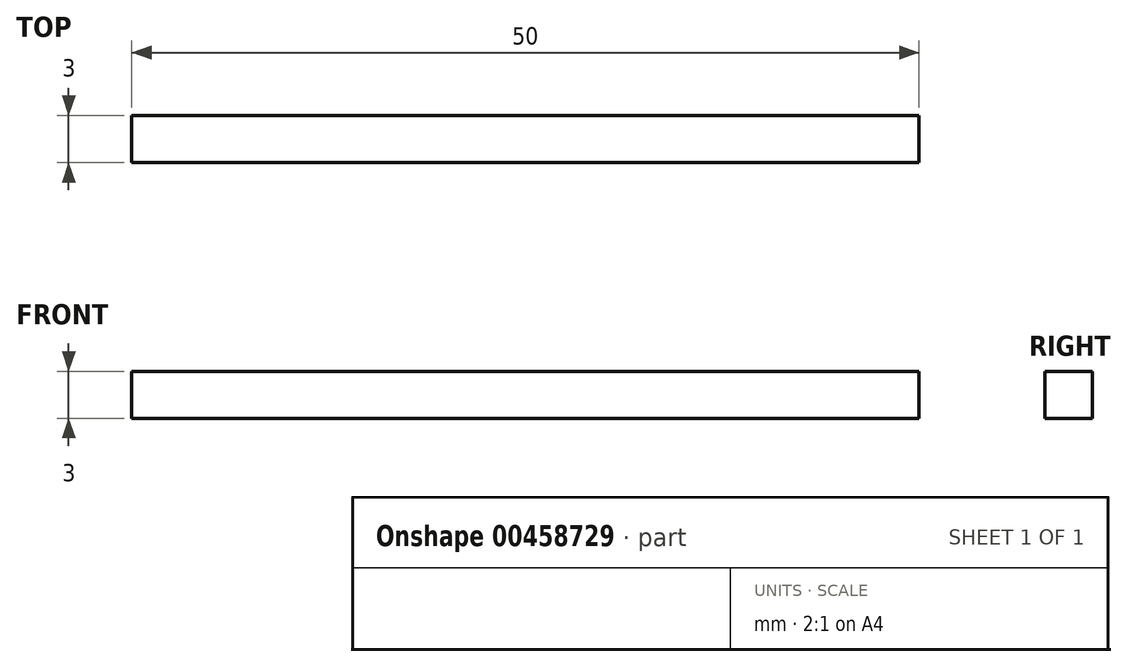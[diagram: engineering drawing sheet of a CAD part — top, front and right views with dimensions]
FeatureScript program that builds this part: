
annotation { "Feature Type Name" : "Feature", "Feature Type Description" : "" }
export const myFeature = defineFeature(function(context is Context, id is Id, definition is map)
    precondition{}
    {
        {
            var Q0;
            Q0=qCreatedBy(makeId("Top.planeOp"),FACE);
            var sketch = newSketch(context, id + "F0", { "sketchPlane" : qUnion([Q0])});
            skLineSegment(sketch, "E0.bottom", {"start": v(-4.45, 1.92) * mm, "end": v(45.55, 1.92) * mm});
            skLineSegment(sketch, "E0.top", {"start": v(-4.45, -1.08) * mm, "end": v(45.55, -1.08) * mm});
            skLineSegment(sketch, "E0.left", {"start": v(-4.45, 1.92) * mm, "end": v(-4.45, -1.08) * mm});
            skLineSegment(sketch, "E0.right", {"start": v(45.55, 1.92) * mm, "end": v(45.55, -1.08) * mm});
            skSolve(sketch);
        }
        {
            var Q0;
            Q0 = qSketchRegion(id + "F0", true);
            extrude(context, id + "F1", {"entities" : qUnion([Q0]), "depth" : 3 * mm, "offsetDistance" : 25 * mm});
        }
    });
